# Revit family: Handshower-American_Standard-Modern-1660.637
name_source: partatom
category: Plumbing Fixtures
revit_build: Autodesk Revit 2018 (Build: 20170223_1515(x64)
units: mm (PartAtom-declared; Revit-internal decimal feet)

## family parameters
Always vertical = No
Cut with Voids When Loaded = No
OmniClass Number = 23.45.05.14.17
OmniClass Title = Showers
Part Type = Normal
Room Calculation Point = No
Round Connector Dimension = Use Diameter
Shared = Yes
Work Plane-Based = Yes

## types (2) — shared parameters
Assembly Code = D2010710
CW Connection = Yes
CWFU = 3
Default Elevation = 0"
Description = Attractive in more ways than one. This stylish multi-function handshower goes well with modern and casual bathrooms. Choose the spray that suits your mood: full spray, full spray/massage combo, pulsating massage, massage/mist or power mist.
Flow Rate = 2.5gpm/9.5L/min.
HW Connection = Yes
HWFU = 3
Height = 9 7/8"
IAPMO Compliance = ASME A112.18.1, CSA 125.1
Length = 3 3/4"
Manufacturer = American Standard
Price = Prices may vary. Please consult Manufacturer Representative for most up-to-date price list.
Product Documentation Link = https://www.americanstandard-us.com
Product Page URL = https://www.americanstandard-us.com
URL = https://www.americanstandard-us.com
Vent Connection = No
WFU = 4
Warranty Information URL = https://www.americanstandard-us.com
Waste Connection = No
Water Connection Diameter = 1/2"
Water Connection Radius = 1/4"
Width = 3"

## per-type parameters (varying)
| type | Finish | Material |
| 1660.637.002 | Metal-American Standard-Brass-002-Polished Chrome | Metal-American Standard-Brass-002-Polished Chrome |
| 1660.637.295 | Metal-American Standard-Brass-295-Brushed Nickel | Metal-American Standard-Brass-295-Brushed Nickel |

note: column(s) folded — value = type name in every type: Model

## geometry (parser evidence)
native form markers: Sweep x2
no freeform markers — native parametric forms only
